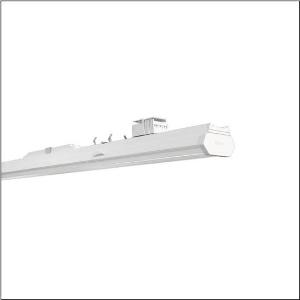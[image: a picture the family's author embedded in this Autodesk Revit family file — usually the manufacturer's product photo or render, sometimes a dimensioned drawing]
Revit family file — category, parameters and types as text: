
# Revit family: licross_r__11_protected_ho_51tp13dn4f5s_0b0f
name_source: partatom
category: Lighting Fixtures
units: mm (PartAtom-declared; Revit-internal decimal feet)

## family parameters
Cut with Voids When Loaded = No
Host = Face
Light Source = No
Part Type = Normal
Room Calculation Point = No
Round Connector Dimension = Use Diameter
Shared = No

## types (1)
- --- (1 x LED, 15550 lm, 87.3 W, 4000K)
    Apparent Load = 87 VA
    CIE Flux Codes = 89 96 99 100 99
    Color Rendering = 80
    Color Temperature = 4000K
    Default Elevation = 1800 mm
    Description = Licross® 11 Protected HO, luminaire insert, of sheet steel, galvanised, coil coated, white, length: 1.500mm, width: 90mm, height: 101mm, LED rated luminous flux: 15.550lm, light colour: 840, control gear: DALI 2, with plug, 5-pole, with phase selection, mains connection: 220..240V, AC, 50/60Hz, rated input power: 87W, halogen-free wiring, primary light control with lens, of plastic, primary optical cover: cover, of PMMA, light emission: direct distribution, primary light characteristic: symmetric, protection rating (complete): IP64, insulation class (complete): insulation class I (protective earthing), certification: CE, ENEC, VDE, UKCA, protection symbol: D if used in an environment with conductive dust loads with corresponding accessories, impact resistance: IK06, permissible ambient temperature for indoor applications: -25..+30°C, corresponds to IFS (International Featured Standards) requirements for safety and quality in the food industry, reducing of maximum allowable ambient temperature of 5°C with ceiling mounting, LABS conformity tested according to VDMA 24364:2018-05, packaging unit: 1 piece
    Height = 92 mm
    Lamp = 1 x LED
    Lamp Light Flux = 15550 lm
    Lamp Power = 87.3 W
    Lamp count = 1
    Length = 1500 mm
    Luminous efficacy = 178 lm/W
    Manufacturer = Siteco
    ModVariant = No
    Model = 51TP13DN4F5S
    Mounting Place = Ceiling
    Mounting Type = Pendant
    Number of Poles = 1
    OnlyDefault = Yes
    Power Factor = 1
    Product Name = Licross® 11 Protected HO
    Product group = luminaire insert
    ProductGroupID = 901
    Protection Class = Protection class I
    Protection Degree = IP 64
    RLX_Detail_Level = 1
    RLX_Emergency_Light_Flux = 0 lm
    RLX_Emergency_Type = 0
    RLX_Emergency_Type_DB = No
    RlxData = <blob elided: 24313 chars, md5=c70294ac>
    Socket = socket
    Standby Power = 0 W
    System Light Flux = 15550 lm
    System Power = 87 W
    Type Comments = factory setting: luminous flux: 100 % | dim-lin: 254 | 589 mA
    Type Image = l_1256148.jpg
    URL = http://relux.com
    VarID = @adj_030973
    Voltage = 0 V
    Weight = 0.00 kg
    Width = 88 mm

## geometry (parser evidence)
native form markers: Blend x4, Sweep x11
no freeform markers — native parametric forms only
